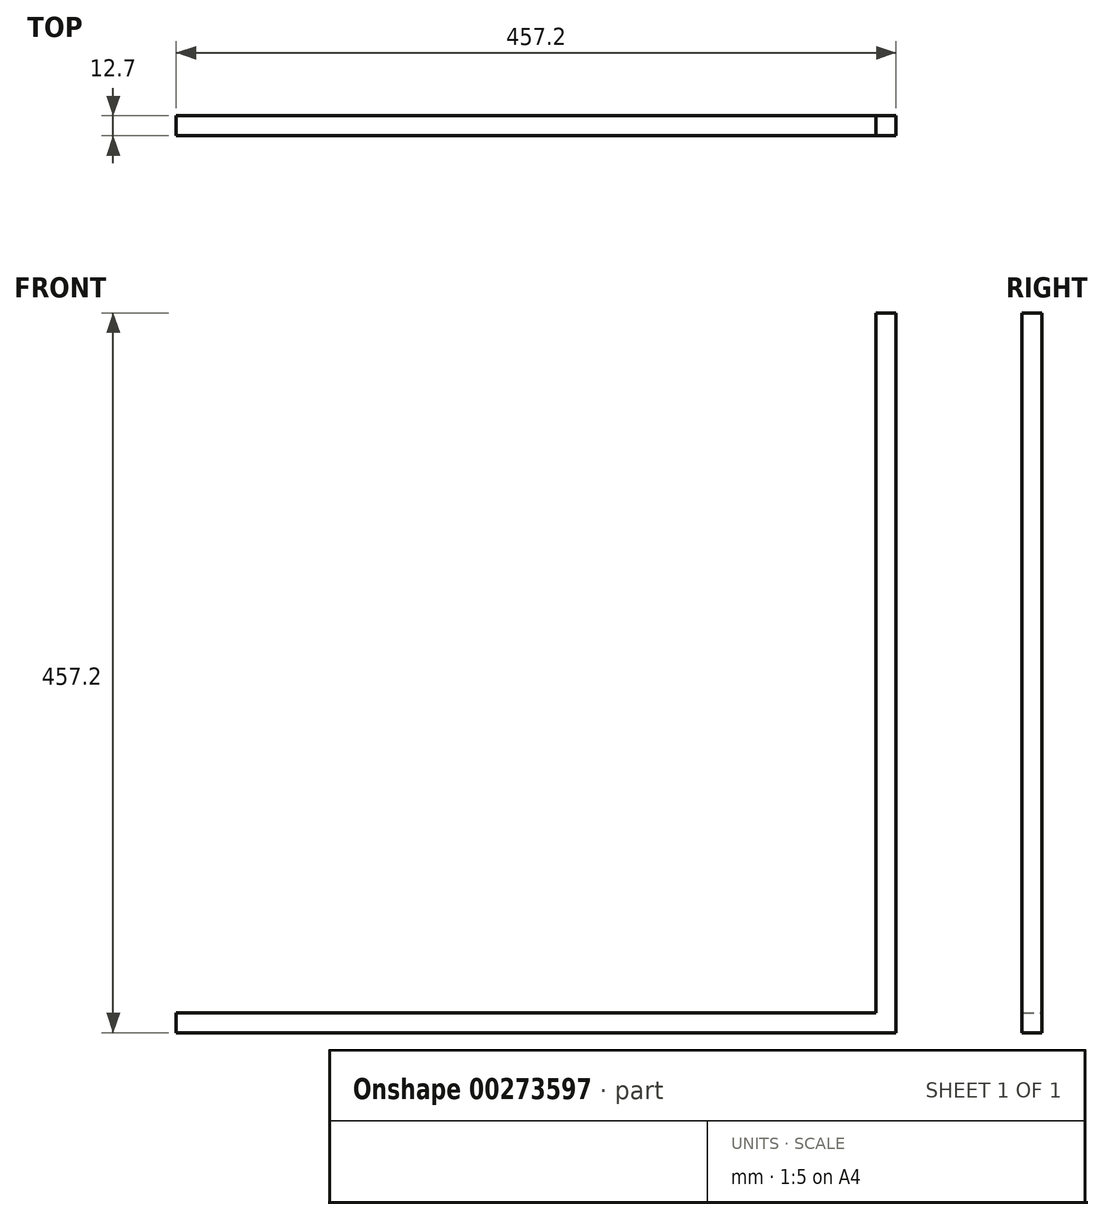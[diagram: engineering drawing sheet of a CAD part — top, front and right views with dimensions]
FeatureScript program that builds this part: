
annotation { "Feature Type Name" : "Feature", "Feature Type Description" : "" }
export const myFeature = defineFeature(function(context is Context, id is Id, definition is map)
    precondition{}
    {
        {
            var Q0;
            Q0=qCreatedBy(makeId("Top.planeOp"),FACE);
            var sketch = newSketch(context, id + "F0", { "sketchPlane" : qUnion([Q0])});
            skLineSegment(sketch, "E0.bottom", {"start": v(0, 0) * mm, "end": v(457.2, 0) * mm});
            skLineSegment(sketch, "E0.top", {"start": v(0, -12.7) * mm, "end": v(457.2, -12.7) * mm});
            skLineSegment(sketch, "E0.left", {"start": v(0, 0) * mm, "end": v(0, -12.7) * mm});
            skLineSegment(sketch, "E0.right", {"start": v(457.2, 0) * mm, "end": v(457.2, -12.7) * mm});
            skLineSegment(sketch, "E1.bottom", {"start": v(457.2, 0) * mm, "end": v(444.5, 0) * mm});
            skLineSegment(sketch, "E1.top", {"start": v(457.2, 444.5) * mm, "end": v(444.5, 444.5) * mm});
            skLineSegment(sketch, "E1.left", {"start": v(457.2, 0) * mm, "end": v(457.2, 444.5) * mm});
            skLineSegment(sketch, "E1.right", {"start": v(444.5, 0) * mm, "end": v(444.5, 444.5) * mm});
            skSolve(sketch);
        }
        {
            var Q0;
            Q0=makeQuery(id+"F0.imprint","IMPRINT",FACE,{"disambiguationData":[TD([[makeQuery(id+"F0.imprint","IMPRINT",EDGE,{"derivedFrom":sQuery(id+"F0.wireOp",EDGE,"E1.bottom")}),-1.0]])]});
            var Q1;
            Q1=makeQuery(id+"F0.imprint","IMPRINT",FACE,{"disambiguationData":[TD([[makeQuery(id+"F0.imprint","IMPRINT",EDGE,{"derivedFrom":sQuery(id+"F0.wireOp",EDGE,"E0.bottom")}),-1.0]])]});
            extrude(context, id + "F1", {"entities" : qUnion([Q0, Q1]), "depth" : 12.7 * mm});
        }
        {
            var Q0;
            Q0=makeQuery(id+"F1.opExtrude","CAP_FACE",FACE,{"disambiguationData":[OSD([sQuery(id+"F0.wireOp",EDGE,"E0.bottom"),sQuery(id+"F0.wireOp",EDGE,"E0.top"),sQuery(id+"F0.wireOp",EDGE,"E0.left"),sQuery(id+"F0.wireOp",EDGE,"E0.right"),sQuery(id+"F0.wireOp",EDGE,"E1.top"),sQuery(id+"F0.wireOp",EDGE,"E1.left"),sQuery(id+"F0.wireOp",EDGE,"E1.right")])],"isStart":false});
            var sketch = newSketch(context, id + "F2", { "sketchPlane" : qUnion([Q0])});
            skLineSegment(sketch, "E2.bottom", {"start": v(457.2, -12.7) * mm, "end": v(444.5, -12.7) * mm});
            skLineSegment(sketch, "E2.top", {"start": v(457.2, 0) * mm, "end": v(444.5, 0) * mm});
            skLineSegment(sketch, "E2.left", {"start": v(457.2, -12.7) * mm, "end": v(457.2, 0) * mm});
            skLineSegment(sketch, "E2.right", {"start": v(444.5, -12.7) * mm, "end": v(444.5, 0) * mm});
            skSolve(sketch);
        }
        {
            var Q0;
            Q0=makeQuery(id+"F2.imprint","IMPRINT",FACE,{"disambiguationData":[TD([[makeQuery(id+"F2.imprint","IMPRINT",EDGE,{"derivedFrom":sQuery(id+"F2.wireOp",EDGE,"E2.bottom")}),1.0]])]});
            extrude(context, id + "F3", {"entities" : qUnion([Q0]), "operationType" : NewBodyOperationType.ADD, "depth" : 444.5 * mm});
        }
    });
